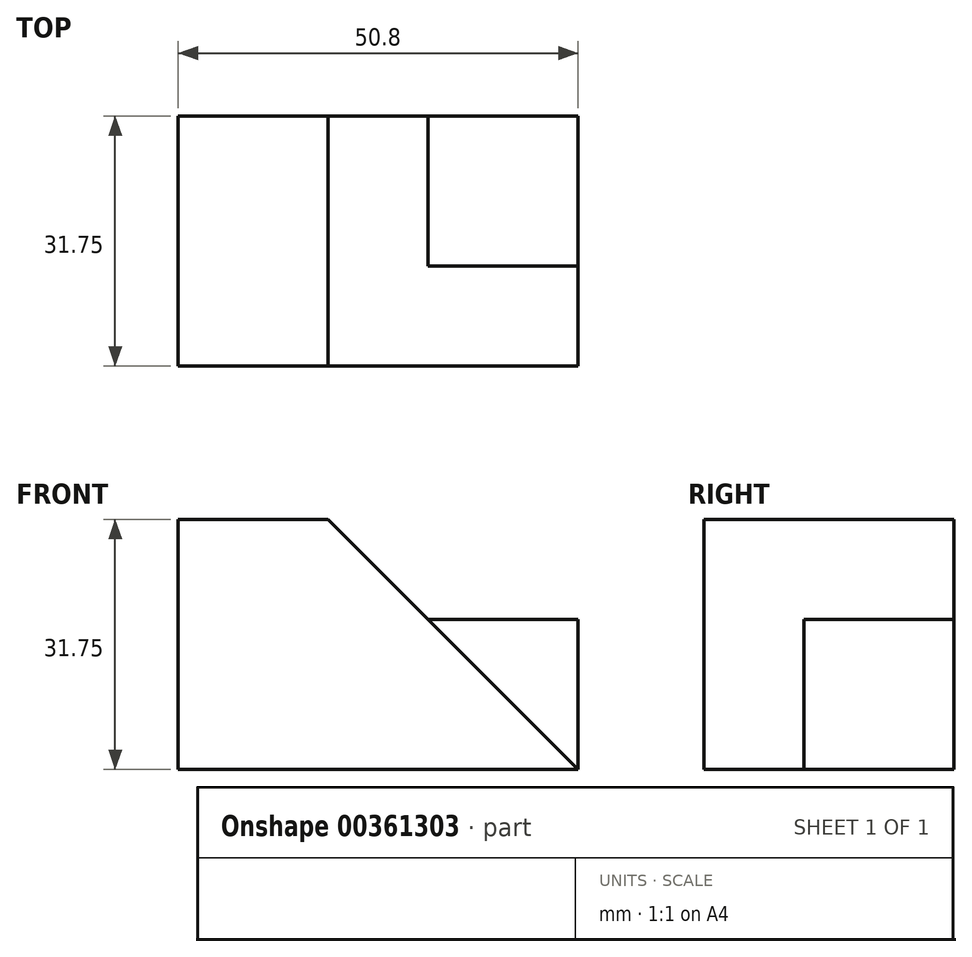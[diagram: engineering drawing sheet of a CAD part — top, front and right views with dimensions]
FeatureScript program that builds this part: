
annotation { "Feature Type Name" : "Feature", "Feature Type Description" : "" }
export const myFeature = defineFeature(function(context is Context, id is Id, definition is map)
    precondition{}
    {
        {
            var Q0;
            Q0=qCreatedBy(makeId("Front.planeOp"),FACE);
            var sketch = newSketch(context, id + "F0", { "sketchPlane" : qUnion([Q0])});
            skLineSegment(sketch, "E0", {"start": v(0, 0) * mm, "end": v(0, 31.75) * mm});
            skLineSegment(sketch, "E1", {"start": v(0, 31.75) * mm, "end": v(19.05, 31.75) * mm});
            skLineSegment(sketch, "E2", {"start": v(19.05, 31.75) * mm, "end": v(50.8, 0) * mm});
            skLineSegment(sketch, "E3", {"start": v(50.8, 0) * mm, "end": v(0, 0) * mm});
            skSolve(sketch);
        }
        {
            var Q0;
            Q0 = qSketchRegion(id + "F0", true);
            extrude(context, id + "F1", {"entities" : qUnion([Q0]), "oppositeDirection" : true, "depth" : 31.75 * mm});
        }
        {
            var Q0;
            Q0=makeQuery(id+"F1.opExtrude","CAP_FACE",FACE,{"disambiguationData":[OSD([sQuery(id+"F0.wireOp",EDGE,"E0"),sQuery(id+"F0.wireOp",EDGE,"E1"),sQuery(id+"F0.wireOp",EDGE,"E2"),sQuery(id+"F0.wireOp",EDGE,"E3")])],"isStart":false});
            var sketch = newSketch(context, id + "F2", { "sketchPlane" : qUnion([Q0])});
            skLineSegment(sketch, "E4", {"start": v(-50.8, 0) * mm, "end": v(-50.8, 19.05) * mm});
            skLineSegment(sketch, "E5", {"start": v(-50.8, 19.05) * mm, "end": v(-31.75, 19.05) * mm});
            skLineSegment(sketch, "E6", {"start": v(-31.75, 19.05) * mm, "end": v(-50.8, 0) * mm});
            skSolve(sketch);
        }
        {
            var Q0;
            Q0=makeQuery(id+"F2.imprint","IMPRINT",FACE,{"disambiguationData":[TD([[makeQuery(id+"F2.imprint","IMPRINT",EDGE,{"derivedFrom":sQuery(id+"F2.wireOp",EDGE,"E4")}),-1.0]])]});
            extrude(context, id + "F3", {"entities" : qUnion([Q0]), "oppositeDirection" : true, "depth" : 19.05 * mm});
        }
    });
